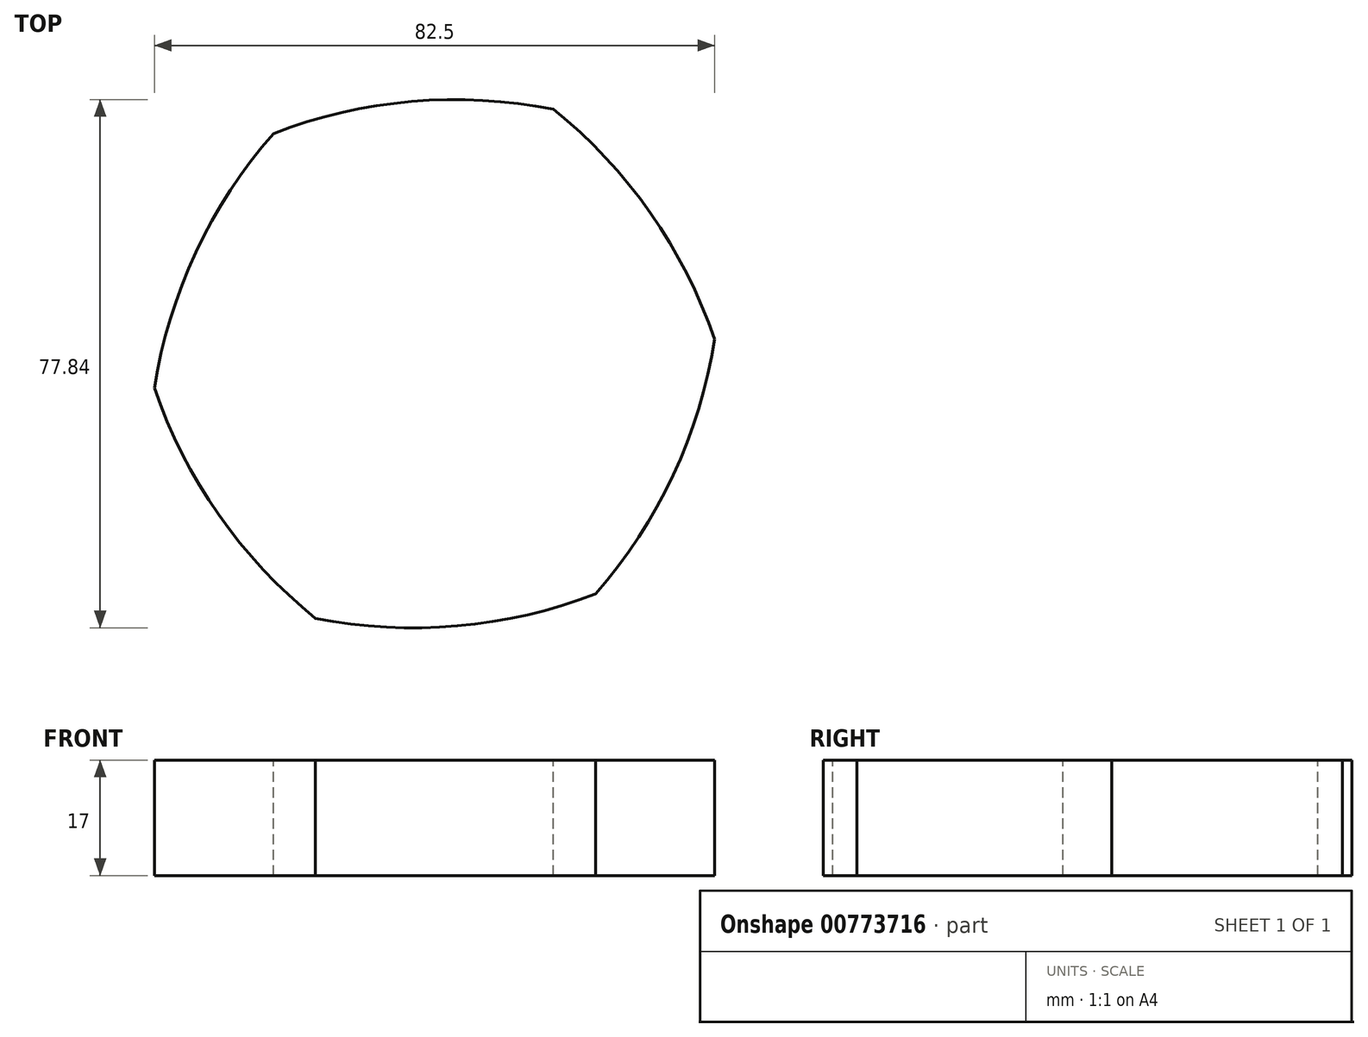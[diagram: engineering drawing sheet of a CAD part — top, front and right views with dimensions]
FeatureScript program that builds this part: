
annotation { "Feature Type Name" : "Feature", "Feature Type Description" : "" }
export const myFeature = defineFeature(function(context is Context, id is Id, definition is map)
    precondition{}
    {
        {
            var Q0;
            Q0=qCreatedBy(makeId("Top.planeOp"),FACE);
            var sketch = newSketch(context, id + "F0", { "sketchPlane" : qUnion([Q0])});
            skPoint(sketch, "E0.0.midPoint", {"position": v(-32.5, 15.17) * mm});
            skArc(sketch, "E1", {"start": v(23.73, -33.93) * mm, "mid": v(35.15, -16.41) * mm, "end": v(41.25, 3.59) * mm});
            skArc(sketch, "E2", {"start": v(41.25, 3.59) * mm, "mid": v(31.79, 22.23) * mm, "end": v(17.52, 37.52) * mm});
            skArc(sketch, "E3", {"start": v(17.52, 37.52) * mm, "mid": v(-3.36, 38.64) * mm, "end": v(-23.73, 33.93) * mm});
            skArc(sketch, "E4", {"start": v(-23.73, 33.93) * mm, "mid": v(-35.15, 16.41) * mm, "end": v(-41.25, -3.59) * mm});
            skArc(sketch, "E5", {"start": v(-41.25, -3.59) * mm, "mid": v(-31.79, -22.23) * mm, "end": v(-17.52, -37.52) * mm});
            skPoint(sketch, "E6.orphan", {"position": v(41.25, 3.59) * mm});
            skPoint(sketch, "E0.2.start.orphan", {"position": v(17.52, 37.52) * mm});
            skPoint(sketch, "E7.orphan", {"position": v(23.73, -33.93) * mm});
            skPoint(sketch, "E8.orphan", {"position": v(-17.52, -37.52) * mm});
            skPoint(sketch, "E9.orphan", {"position": v(-41.25, -3.59) * mm});
            skPoint(sketch, "E0.0.end.orphan", {"position": v(-23.73, 33.93) * mm});
            skArc(sketch, "E10.trimOffspring", {"start": v(-17.52, -37.52) * mm, "mid": v(3.36, -38.64) * mm, "end": v(23.73, -33.93) * mm});
            skSolve(sketch);
        }
        {
            var Q0;
            Q0=makeQuery(id+"F0.imprint","IMPRINT",FACE,{"disambiguationData":[TD([[makeQuery(id+"F0.imprint","IMPRINT",EDGE,{"derivedFrom":sQuery(id+"F0.wireOp",EDGE,"E1")}),1.0]])]});
            extrude(context, id + "F1", {"entities" : qUnion([Q0]), "oppositeDirection" : true, "depth" : 17 * mm, "offsetDistance" : 25 * mm});
        }
    });
